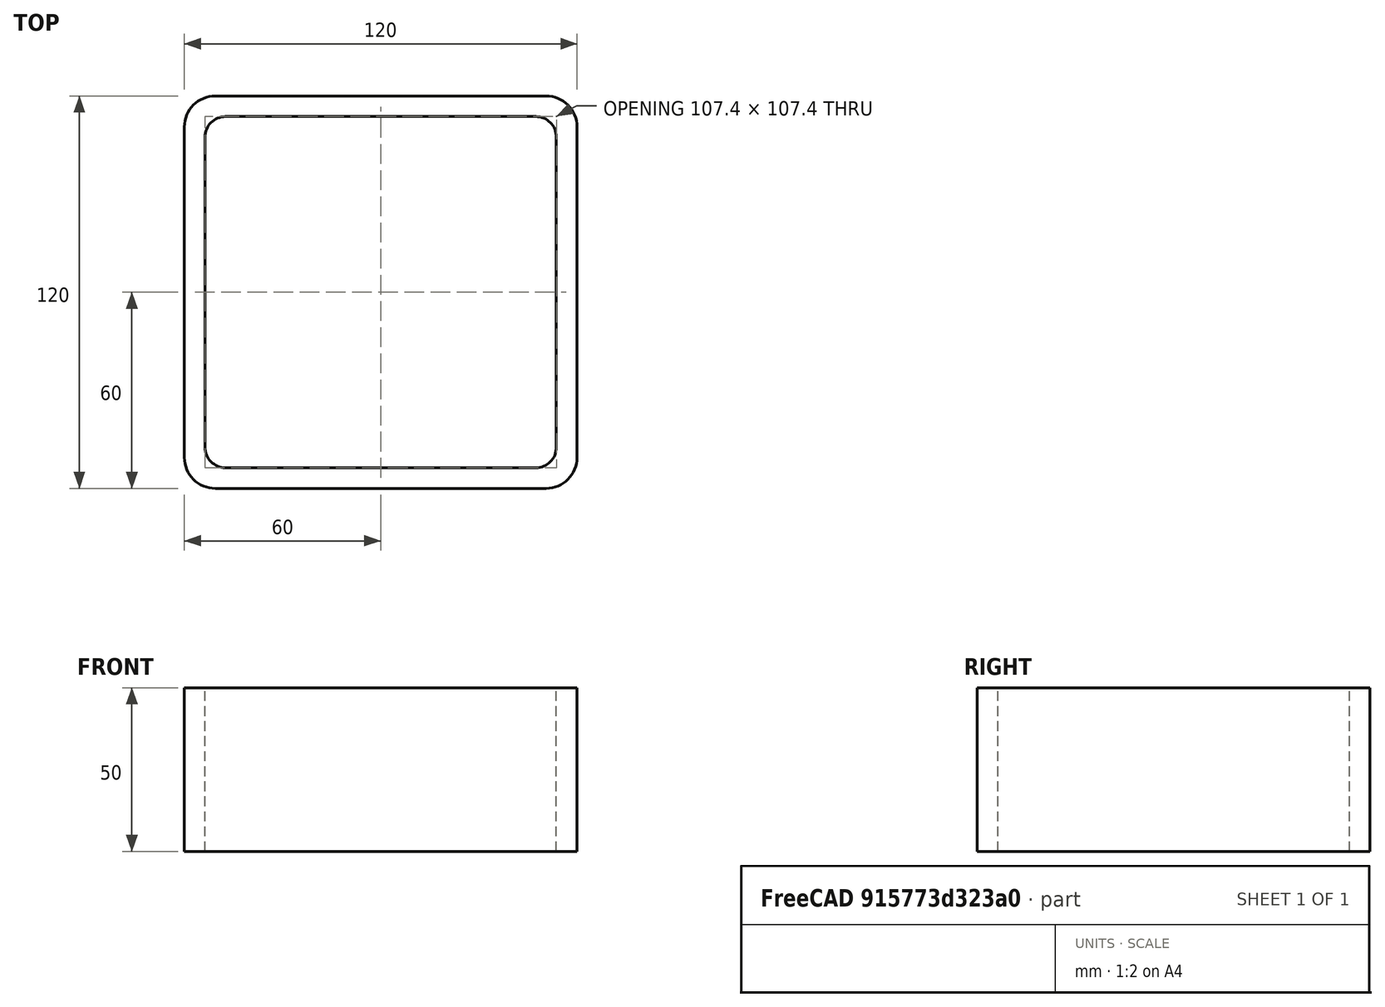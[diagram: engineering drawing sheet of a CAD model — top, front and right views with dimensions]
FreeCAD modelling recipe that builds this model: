
FCSTD DOCUMENT  (FreeCAD 0.15R4671 (Git))
Label: Square hollow section 120x120x6.3 EN10219 S235JRH
License: All rights reserved
LicenseURL: http://en.wikipedia.org/wiki/All_rights_reserved
objects: Sketcher::SketchObject×1, Part::Extrusion×1
note: 2 computed .brp shape members not serialized (recipe doc carries the construction recipe); baked Part::Feature solids carry a one-line shape summary decoded from their .brp

FEATURE [Sketcher::SketchObject] Sketch
  sketch-geometry (16):
    g0: LineSegment StartX=-47.4 StartY=53.7 StartZ=0 EndX=47.4 EndY=53.7 EndZ=0
    g1: LineSegment StartX=53.7 StartY=47.4 StartZ=0 EndX=53.7 EndY=-47.4 EndZ=0
    g2: LineSegment StartX=47.4 StartY=-53.7 StartZ=0 EndX=-47.4 EndY=-53.7 EndZ=0
    g3: LineSegment StartX=-53.7 StartY=-47.4 StartZ=0 EndX=-53.7 EndY=47.4 EndZ=0
    g4: LineSegment StartX=-50.55 StartY=60 StartZ=0 EndX=50.55 EndY=60 EndZ=0
    g5: LineSegment StartX=60 StartY=50.55 StartZ=0 EndX=60 EndY=-50.55 EndZ=0
    g6: LineSegment StartX=50.55 StartY=-60 StartZ=0 EndX=-50.55 EndY=-60 EndZ=0
    g7: LineSegment StartX=-60 StartY=-50.55 StartZ=0 EndX=-60 EndY=50.55 EndZ=0
    g8: ArcOfCircle CenterX=-47.4 CenterY=47.4 CenterZ=0 NormalX=0 NormalY=0 NormalZ=1 Radius=6.3 StartAngle=1.5708 EndAngle=3.14159
    g9: ArcOfCircle CenterX=47.4 CenterY=47.4 CenterZ=0 NormalX=0 NormalY=0 NormalZ=1 Radius=6.3 StartAngle=0 EndAngle=1.5708
    g10: ArcOfCircle CenterX=47.4 CenterY=-47.4 CenterZ=0 NormalX=0 NormalY=0 NormalZ=1 Radius=6.3 StartAngle=4.71239 EndAngle=6.28319
    g11: ArcOfCircle CenterX=-47.4 CenterY=-47.4 CenterZ=0 NormalX=0 NormalY=0 NormalZ=1 Radius=6.3 StartAngle=3.14159 EndAngle=4.71239
    g12: ArcOfCircle CenterX=50.55 CenterY=50.55 CenterZ=0 NormalX=0 NormalY=0 NormalZ=1 Radius=9.45 StartAngle=0 EndAngle=1.5708
    g13: ArcOfCircle CenterX=50.55 CenterY=-50.55 CenterZ=0 NormalX=0 NormalY=0 NormalZ=1 Radius=9.45 StartAngle=4.71239 EndAngle=6.28319
    g14: ArcOfCircle CenterX=-50.55 CenterY=-50.55 CenterZ=0 NormalX=0 NormalY=0 NormalZ=1 Radius=9.45 StartAngle=3.14159 EndAngle=4.71239
    g15: ArcOfCircle CenterX=-50.55 CenterY=50.55 CenterZ=0 NormalX=0 NormalY=0 NormalZ=1 Radius=9.45 StartAngle=1.5708 EndAngle=3.14159
  constraints (36):
    c: Horizontal(g2)
    c: Vertical(g3)
    c: Horizontal(g6)
    c: Vertical(g7)
    c: Tangent(g3,g8) = 1.5708
    c: Tangent(g0,g8) = 1.5708
    c: Tangent(g0,g9) = 1.5708
    c: Tangent(g1,g9) = 1.5708
    c: Tangent(g1,g10) = 1.5708
    c: Tangent(g2,g10) = 1.5708
    c: Tangent(g2,g11) = 1.5708
    c: Tangent(g3,g11) = 1.5708
    c: Tangent(g4,g12) = 1.5708
    c: Tangent(g5,g12) = 1.5708
    c: Tangent(g5,g13) = 1.5708
    c: Tangent(g6,g13) = 1.5708
    c: Tangent(g6,g14) = 1.5708
    c: Tangent(g7,g14) = 1.5708
    c: Tangent(g7,g15) = 1.5708
    c: Tangent(g4,g15) = 1.5708
    c: Equal(g9,g8)
    c: Equal(g9,g11)
    c: Equal(g9,g10)
    c: Equal(g12,g15)
    c: Equal(g12,g14)
    c: Equal(g12,g13)
    c: Symmetric(g4,g6,g-1)
    c: Symmetric(g7,g5,g-2)
    c: DistanceY(g4,g6) = -120
    c: DistanceX(g7,g5) = 120
    c: Symmetric(g3,g1,g-2)
    c: Symmetric(g0,g2,g-1)
    c: DistanceY(g0,g4) = 6.3
    c: DistanceX(g5,g1) = -6.3
    c: Radius(g9) = 6.3
    c: Radius(g12) = 9.45
FEATURE [Part::Extrusion] Extrude  label="Square hollow section 120x120x6.3 EN10219 S235JRH"
  Base = -> Sketch
  Dir = (0,0,50)
  Solid = true
